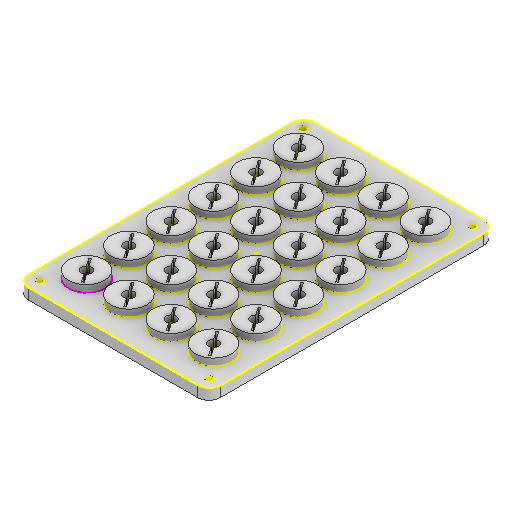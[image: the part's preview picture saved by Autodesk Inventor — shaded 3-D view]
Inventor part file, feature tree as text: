
AUTODESK INVENTOR PART (.ipt)
format: ipt  version: 2022 (Build 260153000, 153)  size: 657,408 bytes
history: native  units: mm
features: projected_geometry x17, sketch x7, extrude x4, hole x2, fillet x1, pattern_linear x1
ambient origin geometry x8: Origin, YZ Plane, XZ Plane, XY Plane, X Axis, Y Axis, Z Axis, Center Point
bodies: Volumenkörper1 (feature_tree)
feature tree (32):
  extrude  "Extrusion1"  Depth=127.5mm
  extrude  "Extrusion2"  Depth=5.0mm
  fillet  "Rundung1"  Radius=16.5mm
  hole  "Bohrung1"  [1 undecoded]
  extrude  "Extrusion3"  Depth=0.85mm
  pattern_linear  "Rechteckige Anordnung2"  Spacing1=0.85mm  [1 undecoded]
  extrude  "Extrusion4"  Depth=6.0mm TaperAngle=0.0deg
  hole  "Bohrung2"  [1 undecoded]
  sketch  "Skizze7"  dims[d25=13.2mm d26=0.85mm d27=6.0mm d28=0.0mm d29=60.0mm d31=18.9mm d32=40.0mm d34=18.9mm d35=13.2mm d36=21.816616mm d37=0.85mm d38=2.0mm d39=0.0mm d40=2.8mm d41=6.0mm d42=4.0mm d43=2.0mm d44=90.0deg d45=8.0mm d46=20.594885mm d30=0.375mm d33=20.594885mm]
  sketch  "Skizze1"  dims[d0=85.5mm d1=127.5mm]
  sketch  "Skizze2"  dims[d2=5.0mm d3=0.0mm d4=16.0mm d5=16.5mm]
  projected_geometry  "Projizierte Kontur1"
  sketch  "Skizze3"  dims[d6=14.4mm d7=3.0mm d8=0.0mm]
  projected_geometry  "Projizierte Kontur2"
  projected_geometry  "Projizierte Kontur3"
  sketch  "Skizze4"  dims[d15=0.85mm d16=13.0mm]
  projected_geometry  "Projizierte Kontur4"
  sketch  "Skizze5"  dims[d17=5.0mm]
  projected_geometry  "Projizierte Kontur5"
  sketch  "Skizze6"  dims[d18=4.6mm d19=6.0mm d20=4.0mm d21=2.0mm d22=90.0deg d23=0.01mm d24=20.594885mm]
  projected_geometry  "Projizierte Kontur6"
  projected_geometry  "Projizierte Kontur7"
  projected_geometry  "Projizierte Kontur8"
  projected_geometry  "Projizierte Kontur9"
  projected_geometry  "Projizierte Kontur10"
  projected_geometry  "Projizierte Kontur11"
  projected_geometry  "Projizierte Kontur12"
  projected_geometry  "Projizierte Kontur13"
  projected_geometry  "Projizierte Kontur14"
  projected_geometry  "Projizierte Kontur15"
  projected_geometry  "Projizierte Kontur16"
  projected_geometry  "Projizierte Kontur17"
note: 3 required parameter values undecoded (feature->parameter linkage not recoverable at this tier; creation-order binding heuristic only, values carry confidence <= 0.55)
